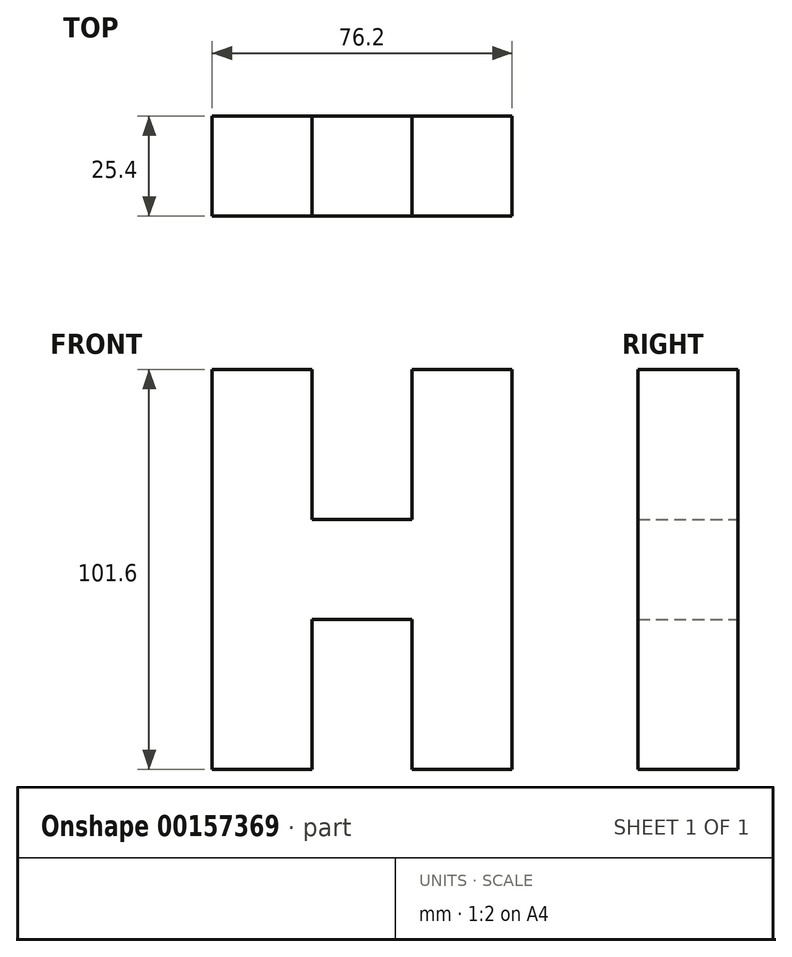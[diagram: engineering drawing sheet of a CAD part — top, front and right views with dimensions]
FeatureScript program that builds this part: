
annotation { "Feature Type Name" : "Feature", "Feature Type Description" : "" }
export const myFeature = defineFeature(function(context is Context, id is Id, definition is map)
    precondition{}
    {
        {
            var Q0;
            Q0=qCreatedBy(makeId("Front.planeOp"),FACE);
            var sketch = newSketch(context, id + "F0", { "sketchPlane" : qUnion([Q0])});
            skLineSegment(sketch, "E0", {"start": v(0, 38.92) * mm, "end": v(0, -39.16) * mm, "construction": true});
            skLineSegment(sketch, "E1", {"start": v(-78.47, 0) * mm, "end": v(39.04, 0) * mm, "construction": true});
            skLineSegment(sketch, "E2", {"start": v(0, 12.7) * mm, "end": v(-12.7, 12.7) * mm});
            skLineSegment(sketch, "E3", {"start": v(-12.7, 12.7) * mm, "end": v(-12.7, 50.8) * mm});
            skLineSegment(sketch, "E4", {"start": v(-12.7, 50.8) * mm, "end": v(-38.1, 50.8) * mm});
            skLineSegment(sketch, "E5", {"start": v(-38.1, 50.8) * mm, "end": v(-38.1, 0) * mm});
            skLineSegment(sketch, "E6.MirrorCS", {"start": v(-38.1, -50.8) * mm, "end": v(-38.1, 0) * mm});
            skLineSegment(sketch, "E7.MirrorCS", {"start": v(-12.7, -50.8) * mm, "end": v(-38.1, -50.8) * mm});
            skLineSegment(sketch, "E8.MirrorCS", {"start": v(-12.7, -12.7) * mm, "end": v(-12.7, -50.8) * mm});
            skLineSegment(sketch, "E9.MirrorCS", {"start": v(0, -12.7) * mm, "end": v(-12.7, -12.7) * mm});
            skLineSegment(sketch, "E10.MirrorCS", {"start": v(0, 12.7) * mm, "end": v(12.7, 12.7) * mm});
            skLineSegment(sketch, "E11.MirrorCS", {"start": v(12.7, 12.7) * mm, "end": v(12.7, 50.8) * mm});
            skLineSegment(sketch, "E12.MirrorCS", {"start": v(12.7, 50.8) * mm, "end": v(38.1, 50.8) * mm});
            skLineSegment(sketch, "E13.MirrorCS", {"start": v(38.1, 50.8) * mm, "end": v(38.1, 0) * mm});
            skLineSegment(sketch, "E14.MirrorCS", {"start": v(38.1, -50.8) * mm, "end": v(38.1, 0) * mm});
            skLineSegment(sketch, "E15.MirrorCS", {"start": v(12.7, -50.8) * mm, "end": v(38.1, -50.8) * mm});
            skLineSegment(sketch, "E16.MirrorCS", {"start": v(12.7, -12.7) * mm, "end": v(12.7, -50.8) * mm});
            skLineSegment(sketch, "E17.MirrorCS", {"start": v(0, -12.7) * mm, "end": v(12.7, -12.7) * mm});
            skSolve(sketch);
        }
        {
            var Q0;
            Q0 = qSketchRegion(id + "F0", true);
            extrude(context, id + "F1", {"entities" : qUnion([Q0]), "depth" : 25.4 * mm});
        }
    });
